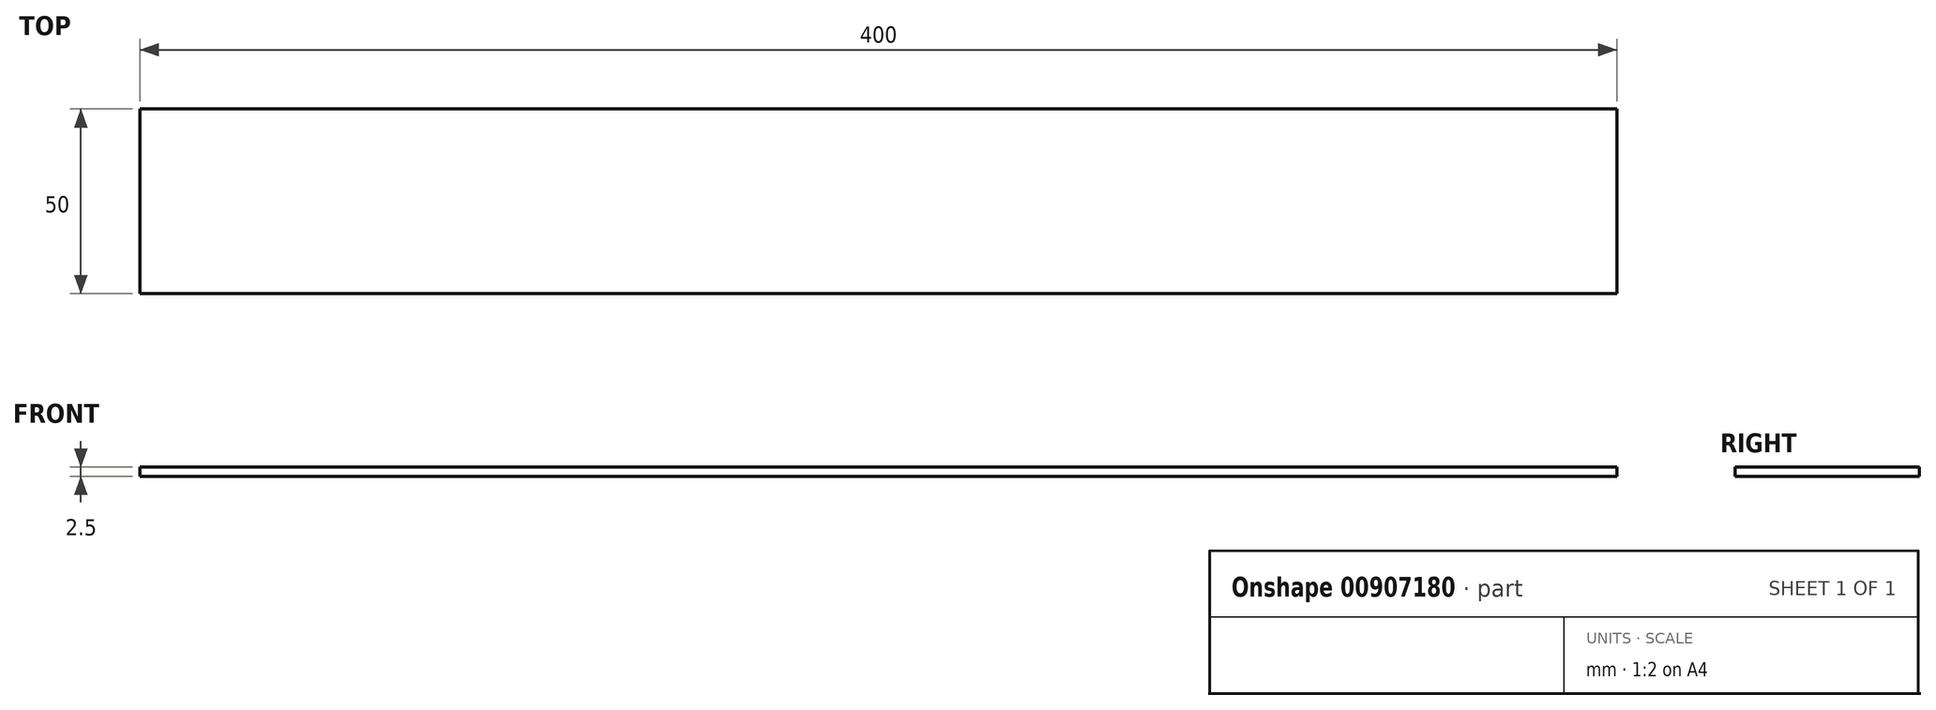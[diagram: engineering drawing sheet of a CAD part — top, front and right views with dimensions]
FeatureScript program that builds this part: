
annotation { "Feature Type Name" : "Feature", "Feature Type Description" : "" }
export const myFeature = defineFeature(function(context is Context, id is Id, definition is map)
    precondition{}
    {
        {
            var Q0;
            Q0=qCreatedBy(makeId("Top.planeOp"),FACE);
            var sketch = newSketch(context, id + "F0", { "sketchPlane" : qUnion([Q0])});
            skLineSegment(sketch, "E0.bottom", {"start": v(-196.64, 32.74) * mm, "end": v(203.36, 32.74) * mm});
            skLineSegment(sketch, "E0.top", {"start": v(-196.64, -17.26) * mm, "end": v(203.36, -17.26) * mm});
            skLineSegment(sketch, "E0.left", {"start": v(-196.64, 32.74) * mm, "end": v(-196.64, -17.26) * mm});
            skLineSegment(sketch, "E0.right", {"start": v(203.36, 32.74) * mm, "end": v(203.36, -17.26) * mm});
            skSolve(sketch);
        }
        {
            var Q0;
            Q0=makeQuery(id+"F0.imprint","IMPRINT",FACE,{"disambiguationData":[TD([[makeQuery(id+"F0.imprint","IMPRINT",EDGE,{"derivedFrom":sQuery(id+"F0.wireOp",EDGE,"E0.bottom")}),-1.0]])]});
            extrude(context, id + "F1", {"entities" : qUnion([Q0]), "depth" : 2.5 * mm, "offsetDistance" : 25 * mm});
        }
    });
